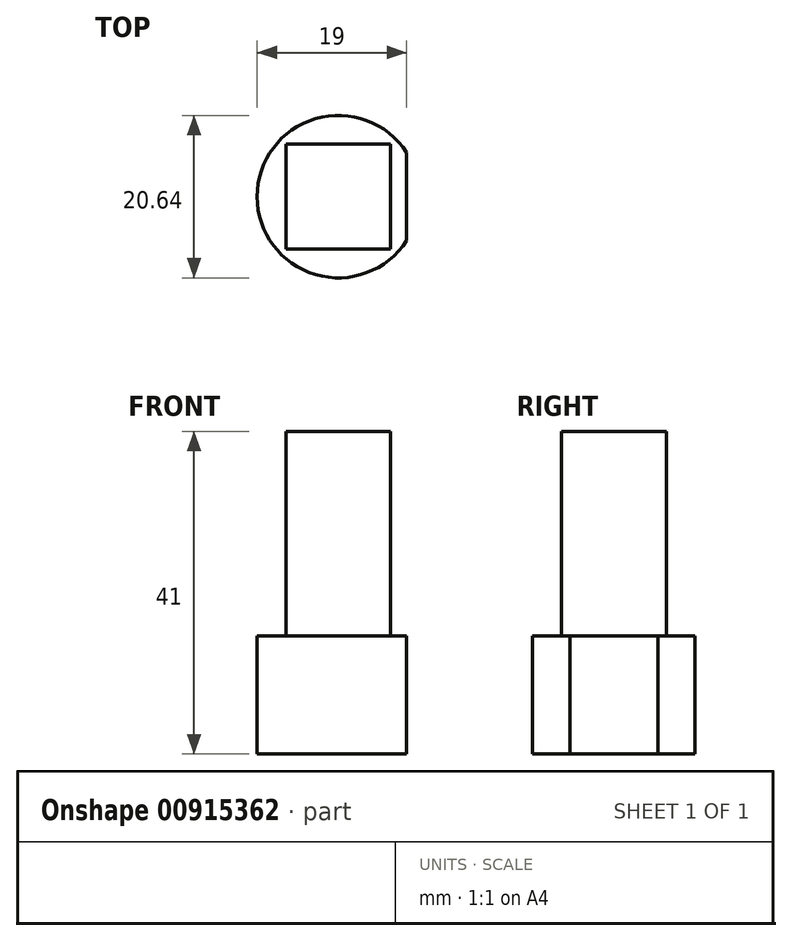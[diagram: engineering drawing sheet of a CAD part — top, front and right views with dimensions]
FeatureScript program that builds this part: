
annotation { "Feature Type Name" : "Feature", "Feature Type Description" : "" }
export const myFeature = defineFeature(function(context is Context, id is Id, definition is map)
    precondition{}
    {
        {
            var Q0;
            Q0=qCreatedBy(makeId("Top.planeOp"),FACE);
            var sketch = newSketch(context, id + "F0", { "sketchPlane" : qUnion([Q0])});
            skCircle(sketch, "E0", {"center": v(0, 0) * mm, "radius": 10.32 * mm});
            skLineSegment(sketch, "E1", {"start": v(8.68, 5.58) * mm, "end": v(8.68, -5.58) * mm});
            skSolve(sketch);
        }
        {
            var Q0;
            {var subQ0=sQuery(id+"F0.wireOp",EDGE,"E1");Q0=makeQuery(id+"F0.imprint","IMPRINT",FACE,{"disambiguationData":[TD([[makeQuery(id+"F0.imprint","IMPRINT",EDGE,{"derivedFrom":subQ0}),-1.0]])]});}
            extrude(context, id + "F1", {"entities" : qUnion([Q0]), "depth" : 15 * mm, "offsetDistance" : 25.4 * mm});
        }
        {
            var Q0;
            Q0=makeQuery(id+"F1.opExtrude","CAP_FACE",FACE,{"disambiguationData":[OSD([sQuery(id+"F0.wireOp",EDGE,"E0"),sQuery(id+"F0.wireOp",EDGE,"E1")])],"isStart":false});
            var sketch = newSketch(context, id + "F2", { "sketchPlane" : qUnion([Q0])});
            skLineSegment(sketch, "E2.bottom", {"start": v(6.65, -6.65) * mm, "end": v(-6.65, -6.65) * mm});
            skLineSegment(sketch, "E2.top", {"start": v(6.65, 6.65) * mm, "end": v(-6.65, 6.65) * mm});
            skLineSegment(sketch, "E2.left", {"start": v(6.65, -6.65) * mm, "end": v(6.65, 6.65) * mm});
            skLineSegment(sketch, "E2.right", {"start": v(-6.65, -6.65) * mm, "end": v(-6.65, 6.65) * mm});
            skPoint(sketch, "E2.middle", {"position": v(0, 0) * mm});
            skSolve(sketch);
        }
        {
            var Q0;
            Q0=makeQuery(id+"F2.imprint","IMPRINT",FACE,{"disambiguationData":[TD([[makeQuery(id+"F2.imprint","IMPRINT",EDGE,{"derivedFrom":sQuery(id+"F2.wireOp",EDGE,"E2.bottom")}),-1.0]])]});
            extrude(context, id + "F3", {"entities" : qUnion([Q0]), "operationType" : NewBodyOperationType.ADD, "depth" : 26 * mm, "offsetDistance" : 25.4 * mm});
        }
    });
